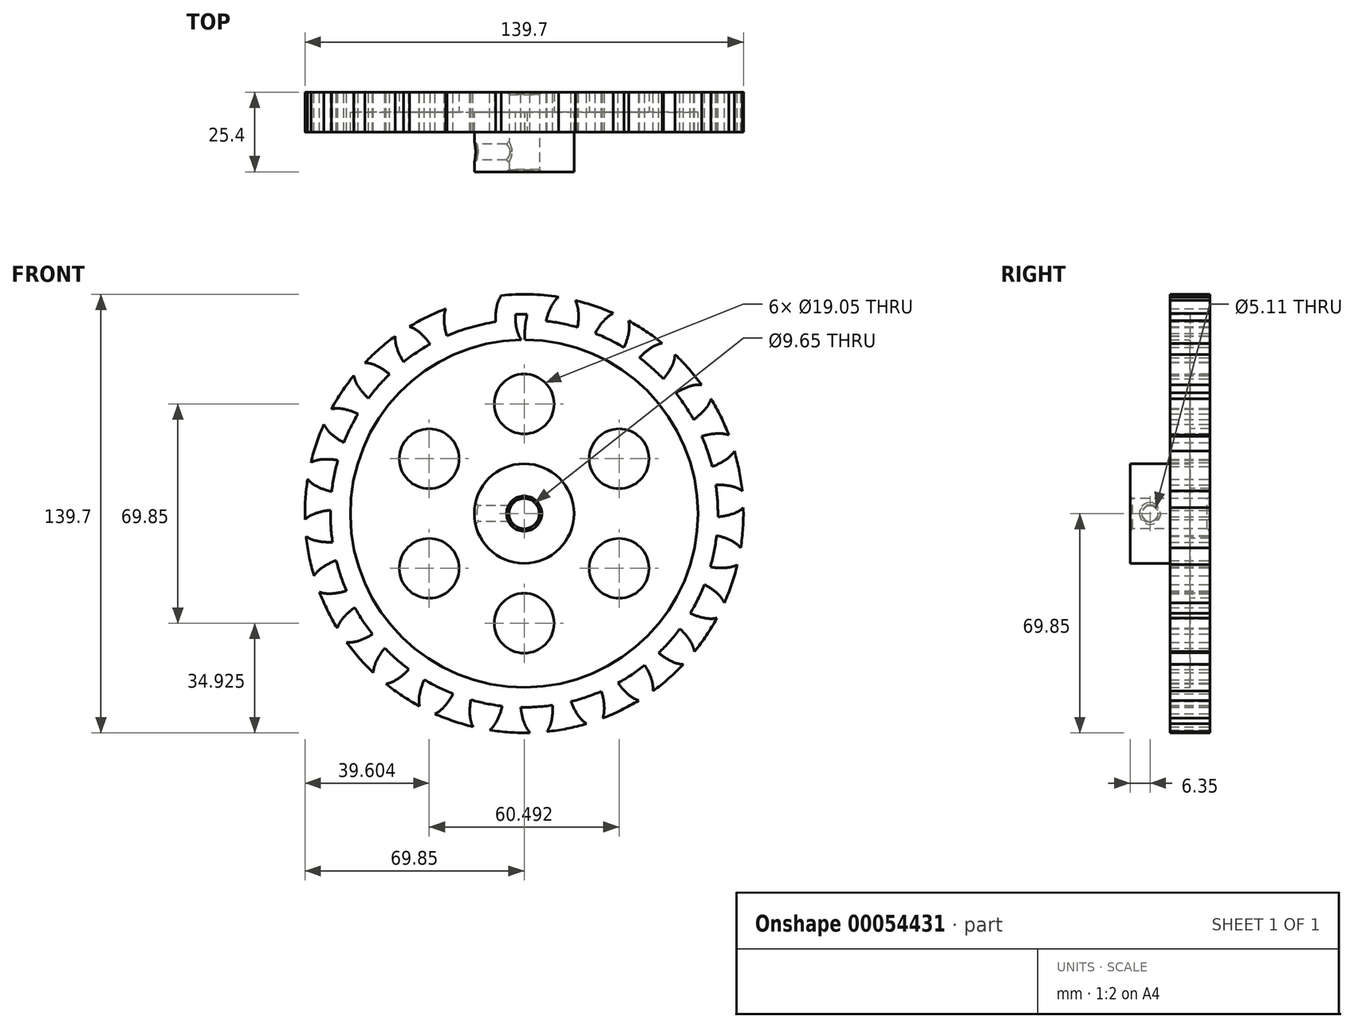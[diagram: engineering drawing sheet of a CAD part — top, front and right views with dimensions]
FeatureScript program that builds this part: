
annotation { "Feature Type Name" : "Feature", "Feature Type Description" : "" }
export const myFeature = defineFeature(function(context is Context, id is Id, definition is map)
    precondition{}
    {
        {
            var Q0;
            Q0=qCreatedBy(makeId("Front.planeOp"),FACE);
            var sketch = newSketch(context, id + "F0", { "sketchPlane" : qUnion([Q0])});
            skCircle(sketch, "E0", {"center": v(0, 0) * mm, "radius": 69.85 * mm});
            skCircle(sketch, "E1", {"center": v(0, 0) * mm, "radius": 66.68 * mm, "construction": true});
            skCircle(sketch, "E2", {"center": v(0, 0) * mm, "radius": 61.72 * mm});
            skLineSegment(sketch, "E3", {"start": v(0, 0) * mm, "end": v(0, 175.81) * mm, "construction": true});
            skLineSegment(sketch, "E4", {"start": v(0, 0) * mm, "end": v(-11.52, 175.81) * mm, "construction": true});
            skLineSegment(sketch, "E5", {"start": v(0, 66.68) * mm, "end": v(-79.4, 66.68) * mm, "construction": true});
            skLineSegment(sketch, "E6", {"start": v(0, 66.68) * mm, "end": v(-79.4, 37.77) * mm, "construction": true});
            skCircle(sketch, "E7", {"center": v(0, 0) * mm, "radius": 62.65 * mm, "construction": true});
            skCircle(sketch, "E8", {"center": v(0, 66.68) * mm, "radius": 13.65 * mm, "construction": true});
            skCircle(sketch, "E9", {"center": v(-12.58, 61.38) * mm, "radius": 13.65 * mm, "construction": true});
            skArc(sketch, "E10", {"start": v(0, 66.68) * mm, "mid": v(-0.78, 68.34) * mm, "end": v(-1.86, 69.83) * mm});
            skArc(sketch, "E11", {"start": v(1.07, 61.71) * mm, "mid": v(0.7, 64.23) * mm, "end": v(0, 66.68) * mm});
            skArc(sketch, "E12.MirrorCS", {"start": v(-8.7, 66.1) * mm, "mid": v(-8.15, 67.86) * mm, "end": v(-7.27, 69.47) * mm});
            skArc(sketch, "E13.MirrorCS", {"start": v(-9.11, 61.05) * mm, "mid": v(-9.07, 63.59) * mm, "end": v(-8.7, 66.1) * mm});
            skArc(sketch, "E14", {"start": v(-2.14, 70.13) * mm, "mid": v(-4.7, 69.8) * mm, "end": v(-7.27, 69.47) * mm});
            skArc(sketch, "E15.1.0", {"start": v(-25.52, 61.6) * mm, "mid": v(-25.43, 63.43) * mm, "end": v(-25, 65.22) * mm});
            skArc(sketch, "E15.1.1", {"start": v(-24.6, 56.6) * mm, "mid": v(-25.22, 59.07) * mm, "end": v(-25.52, 61.6) * mm});
            skArc(sketch, "E15.1.2", {"start": v(-20.22, 67.19) * mm, "mid": v(-22.61, 66.2) * mm, "end": v(-25, 65.22) * mm});
            skArc(sketch, "E15.1.3", {"start": v(-17.26, 64.4) * mm, "mid": v(-18.44, 65.8) * mm, "end": v(-19.87, 66.97) * mm});
            skArc(sketch, "E15.1.4", {"start": v(-14.94, 59.89) * mm, "mid": v(-15.95, 62.22) * mm, "end": v(-17.26, 64.4) * mm});
            skArc(sketch, "E15.2.0", {"start": v(-40.59, 52.9) * mm, "mid": v(-40.98, 54.7) * mm, "end": v(-41.03, 56.53) * mm});
            skArc(sketch, "E15.2.1", {"start": v(-38.41, 48.31) * mm, "mid": v(-39.65, 50.53) * mm, "end": v(-40.59, 52.9) * mm});
            skArc(sketch, "E15.2.2", {"start": v(-36.92, 59.66) * mm, "mid": v(-38.98, 58.1) * mm, "end": v(-41.03, 56.53) * mm});
            skArc(sketch, "E15.2.3", {"start": v(-33.34, 57.74) * mm, "mid": v(-34.84, 58.8) * mm, "end": v(-36.52, 59.54) * mm});
            skArc(sketch, "E15.2.4", {"start": v(-29.93, 53.98) * mm, "mid": v(-31.51, 55.97) * mm, "end": v(-33.34, 57.74) * mm});
            skArc(sketch, "E15.3.0", {"start": v(-52.9, 40.59) * mm, "mid": v(-53.74, 42.22) * mm, "end": v(-54.27, 43.98) * mm});
            skArc(sketch, "E15.3.1", {"start": v(-49.6, 36.72) * mm, "mid": v(-51.38, 38.55) * mm, "end": v(-52.9, 40.59) * mm});
            skArc(sketch, "E15.3.2", {"start": v(-51.1, 48.08) * mm, "mid": v(-52.69, 46.03) * mm, "end": v(-54.27, 43.98) * mm});
            skArc(sketch, "E15.3.3", {"start": v(-47.15, 47.15) * mm, "mid": v(-48.87, 47.77) * mm, "end": v(-50.69, 48.06) * mm});
            skArc(sketch, "E15.3.4", {"start": v(-42.88, 44.4) * mm, "mid": v(-44.93, 45.9) * mm, "end": v(-47.15, 47.15) * mm});
            skArc(sketch, "E15.4.0", {"start": v(-61.6, 25.52) * mm, "mid": v(-62.84, 26.87) * mm, "end": v(-63.8, 28.44) * mm});
            skArc(sketch, "E15.4.1", {"start": v(-57.42, 22.63) * mm, "mid": v(-59.6, 23.94) * mm, "end": v(-61.6, 25.52) * mm});
            skArc(sketch, "E15.4.2", {"start": v(-61.8, 33.21) * mm, "mid": v(-62.8, 30.83) * mm, "end": v(-63.8, 28.44) * mm});
            skArc(sketch, "E15.4.3", {"start": v(-57.74, 33.34) * mm, "mid": v(-59.57, 33.5) * mm, "end": v(-61.4, 33.3) * mm});
            skArc(sketch, "E15.4.4", {"start": v(-52.91, 31.78) * mm, "mid": v(-55.28, 32.72) * mm, "end": v(-57.74, 33.34) * mm});
            skArc(sketch, "E15.5.0", {"start": v(-66.1, 8.7) * mm, "mid": v(-67.65, 9.7) * mm, "end": v(-68.99, 10.96) * mm});
            skArc(sketch, "E15.5.1", {"start": v(-61.32, 7) * mm, "mid": v(-63.77, 7.7) * mm, "end": v(-66.1, 8.7) * mm});
            skArc(sketch, "E15.5.2", {"start": v(-68.3, 16.09) * mm, "mid": v(-68.65, 13.52) * mm, "end": v(-68.99, 10.96) * mm});
            skArc(sketch, "E15.5.3", {"start": v(-64.4, 17.26) * mm, "mid": v(-66.21, 16.94) * mm, "end": v(-67.93, 16.28) * mm});
            skArc(sketch, "E15.5.4", {"start": v(-59.33, 17) * mm, "mid": v(-61.86, 17.3) * mm, "end": v(-64.4, 17.26) * mm});
            skArc(sketch, "E15.6.0", {"start": v(-66.1, -8.7) * mm, "mid": v(-67.86, -8.15) * mm, "end": v(-69.47, -7.27) * mm});
            skArc(sketch, "E15.6.1", {"start": v(-61.05, -9.11) * mm, "mid": v(-63.59, -9.07) * mm, "end": v(-66.1, -8.7) * mm});
            skArc(sketch, "E15.6.2", {"start": v(-70.13, -2.14) * mm, "mid": v(-69.8, -4.7) * mm, "end": v(-69.47, -7.27) * mm});
            skArc(sketch, "E15.6.3", {"start": v(-66.68, 0) * mm, "mid": v(-68.34, -0.78) * mm, "end": v(-69.83, -1.86) * mm});
            skArc(sketch, "E15.6.4", {"start": v(-61.71, 1.07) * mm, "mid": v(-64.23, 0.7) * mm, "end": v(-66.68, 0) * mm});
            skArc(sketch, "E15.7.0", {"start": v(-61.6, -25.52) * mm, "mid": v(-63.43, -25.43) * mm, "end": v(-65.22, -25) * mm});
            skArc(sketch, "E15.7.1", {"start": v(-56.6, -24.6) * mm, "mid": v(-59.07, -25.22) * mm, "end": v(-61.6, -25.52) * mm});
            skArc(sketch, "E15.7.2", {"start": v(-67.19, -20.22) * mm, "mid": v(-66.2, -22.61) * mm, "end": v(-65.22, -25) * mm});
            skArc(sketch, "E15.7.3", {"start": v(-64.4, -17.26) * mm, "mid": v(-65.8, -18.44) * mm, "end": v(-66.97, -19.87) * mm});
            skArc(sketch, "E15.7.4", {"start": v(-59.89, -14.94) * mm, "mid": v(-62.22, -15.95) * mm, "end": v(-64.4, -17.26) * mm});
            skArc(sketch, "E15.8.0", {"start": v(-52.9, -40.59) * mm, "mid": v(-54.7, -40.98) * mm, "end": v(-56.53, -41.03) * mm});
            skArc(sketch, "E15.8.1", {"start": v(-48.31, -38.41) * mm, "mid": v(-50.53, -39.65) * mm, "end": v(-52.9, -40.59) * mm});
            skArc(sketch, "E15.8.2", {"start": v(-59.66, -36.92) * mm, "mid": v(-58.1, -38.98) * mm, "end": v(-56.53, -41.03) * mm});
            skArc(sketch, "E15.8.3", {"start": v(-57.74, -33.34) * mm, "mid": v(-58.8, -34.84) * mm, "end": v(-59.54, -36.52) * mm});
            skArc(sketch, "E15.8.4", {"start": v(-53.98, -29.93) * mm, "mid": v(-55.97, -31.51) * mm, "end": v(-57.74, -33.34) * mm});
            skArc(sketch, "E15.9.0", {"start": v(-40.59, -52.9) * mm, "mid": v(-42.22, -53.74) * mm, "end": v(-43.98, -54.27) * mm});
            skArc(sketch, "E15.9.1", {"start": v(-36.72, -49.6) * mm, "mid": v(-38.55, -51.38) * mm, "end": v(-40.59, -52.9) * mm});
            skArc(sketch, "E15.9.2", {"start": v(-48.08, -51.1) * mm, "mid": v(-46.03, -52.69) * mm, "end": v(-43.98, -54.27) * mm});
            skArc(sketch, "E15.9.3", {"start": v(-47.15, -47.15) * mm, "mid": v(-47.77, -48.87) * mm, "end": v(-48.06, -50.69) * mm});
            skArc(sketch, "E15.9.4", {"start": v(-44.4, -42.88) * mm, "mid": v(-45.9, -44.93) * mm, "end": v(-47.15, -47.15) * mm});
            skArc(sketch, "E15.10.0", {"start": v(-25.52, -61.6) * mm, "mid": v(-26.87, -62.84) * mm, "end": v(-28.44, -63.8) * mm});
            skArc(sketch, "E15.10.1", {"start": v(-22.63, -57.42) * mm, "mid": v(-23.94, -59.6) * mm, "end": v(-25.52, -61.6) * mm});
            skArc(sketch, "E15.10.2", {"start": v(-33.21, -61.8) * mm, "mid": v(-30.83, -62.8) * mm, "end": v(-28.44, -63.8) * mm});
            skArc(sketch, "E15.10.3", {"start": v(-33.34, -57.74) * mm, "mid": v(-33.5, -59.57) * mm, "end": v(-33.3, -61.4) * mm});
            skArc(sketch, "E15.10.4", {"start": v(-31.78, -52.91) * mm, "mid": v(-32.72, -55.28) * mm, "end": v(-33.34, -57.74) * mm});
            skArc(sketch, "E15.11.0", {"start": v(-8.7, -66.1) * mm, "mid": v(-9.7, -67.65) * mm, "end": v(-10.96, -68.99) * mm});
            skArc(sketch, "E15.11.1", {"start": v(-7, -61.32) * mm, "mid": v(-7.7, -63.77) * mm, "end": v(-8.7, -66.1) * mm});
            skArc(sketch, "E15.11.2", {"start": v(-16.09, -68.3) * mm, "mid": v(-13.52, -68.65) * mm, "end": v(-10.96, -68.99) * mm});
            skArc(sketch, "E15.11.3", {"start": v(-17.26, -64.4) * mm, "mid": v(-16.94, -66.21) * mm, "end": v(-16.28, -67.93) * mm});
            skArc(sketch, "E15.11.4", {"start": v(-17, -59.33) * mm, "mid": v(-17.3, -61.86) * mm, "end": v(-17.26, -64.4) * mm});
            skArc(sketch, "E15.12.0", {"start": v(8.7, -66.1) * mm, "mid": v(8.15, -67.86) * mm, "end": v(7.27, -69.47) * mm});
            skArc(sketch, "E15.12.1", {"start": v(9.11, -61.05) * mm, "mid": v(9.07, -63.59) * mm, "end": v(8.7, -66.1) * mm});
            skArc(sketch, "E15.12.2", {"start": v(2.14, -70.13) * mm, "mid": v(4.7, -69.8) * mm, "end": v(7.27, -69.47) * mm});
            skArc(sketch, "E15.12.3", {"start": v(0, -66.68) * mm, "mid": v(0.78, -68.34) * mm, "end": v(1.86, -69.83) * mm});
            skArc(sketch, "E15.12.4", {"start": v(-1.07, -61.71) * mm, "mid": v(-0.7, -64.23) * mm, "end": v(0, -66.68) * mm});
            skArc(sketch, "E15.13.0", {"start": v(25.52, -61.6) * mm, "mid": v(25.43, -63.43) * mm, "end": v(25, -65.22) * mm});
            skArc(sketch, "E15.13.1", {"start": v(24.6, -56.6) * mm, "mid": v(25.22, -59.07) * mm, "end": v(25.52, -61.6) * mm});
            skArc(sketch, "E15.13.2", {"start": v(20.22, -67.19) * mm, "mid": v(22.61, -66.2) * mm, "end": v(25, -65.22) * mm});
            skArc(sketch, "E15.13.3", {"start": v(17.26, -64.4) * mm, "mid": v(18.44, -65.8) * mm, "end": v(19.87, -66.97) * mm});
            skArc(sketch, "E15.13.4", {"start": v(14.94, -59.89) * mm, "mid": v(15.95, -62.22) * mm, "end": v(17.26, -64.4) * mm});
            skArc(sketch, "E15.14.0", {"start": v(40.59, -52.9) * mm, "mid": v(40.98, -54.7) * mm, "end": v(41.03, -56.53) * mm});
            skArc(sketch, "E15.14.1", {"start": v(38.41, -48.31) * mm, "mid": v(39.65, -50.53) * mm, "end": v(40.59, -52.9) * mm});
            skArc(sketch, "E15.14.2", {"start": v(36.92, -59.66) * mm, "mid": v(38.98, -58.1) * mm, "end": v(41.03, -56.53) * mm});
            skArc(sketch, "E15.14.3", {"start": v(33.34, -57.74) * mm, "mid": v(34.84, -58.8) * mm, "end": v(36.52, -59.54) * mm});
            skArc(sketch, "E15.14.4", {"start": v(29.93, -53.98) * mm, "mid": v(31.51, -55.97) * mm, "end": v(33.34, -57.74) * mm});
            skArc(sketch, "E15.15.0", {"start": v(52.9, -40.59) * mm, "mid": v(53.74, -42.22) * mm, "end": v(54.27, -43.98) * mm});
            skArc(sketch, "E15.15.1", {"start": v(49.6, -36.72) * mm, "mid": v(51.38, -38.55) * mm, "end": v(52.9, -40.59) * mm});
            skArc(sketch, "E15.15.2", {"start": v(51.1, -48.08) * mm, "mid": v(52.69, -46.03) * mm, "end": v(54.27, -43.98) * mm});
            skArc(sketch, "E15.15.3", {"start": v(47.15, -47.15) * mm, "mid": v(48.87, -47.77) * mm, "end": v(50.69, -48.06) * mm});
            skArc(sketch, "E15.15.4", {"start": v(42.88, -44.4) * mm, "mid": v(44.93, -45.9) * mm, "end": v(47.15, -47.15) * mm});
            skArc(sketch, "E15.16.0", {"start": v(61.6, -25.52) * mm, "mid": v(62.84, -26.87) * mm, "end": v(63.8, -28.44) * mm});
            skArc(sketch, "E15.16.1", {"start": v(57.42, -22.63) * mm, "mid": v(59.6, -23.94) * mm, "end": v(61.6, -25.52) * mm});
            skArc(sketch, "E15.16.2", {"start": v(61.8, -33.21) * mm, "mid": v(62.8, -30.83) * mm, "end": v(63.8, -28.44) * mm});
            skArc(sketch, "E15.16.3", {"start": v(57.74, -33.34) * mm, "mid": v(59.57, -33.5) * mm, "end": v(61.4, -33.3) * mm});
            skArc(sketch, "E15.16.4", {"start": v(52.91, -31.78) * mm, "mid": v(55.28, -32.72) * mm, "end": v(57.74, -33.34) * mm});
            skArc(sketch, "E15.17.0", {"start": v(66.1, -8.7) * mm, "mid": v(67.65, -9.7) * mm, "end": v(68.99, -10.96) * mm});
            skArc(sketch, "E15.17.1", {"start": v(61.32, -7) * mm, "mid": v(63.77, -7.7) * mm, "end": v(66.1, -8.7) * mm});
            skArc(sketch, "E15.17.2", {"start": v(68.3, -16.09) * mm, "mid": v(68.65, -13.52) * mm, "end": v(68.99, -10.96) * mm});
            skArc(sketch, "E15.17.3", {"start": v(64.4, -17.26) * mm, "mid": v(66.21, -16.94) * mm, "end": v(67.93, -16.28) * mm});
            skArc(sketch, "E15.17.4", {"start": v(59.33, -17) * mm, "mid": v(61.86, -17.3) * mm, "end": v(64.4, -17.26) * mm});
            skArc(sketch, "E15.18.0", {"start": v(66.1, 8.7) * mm, "mid": v(67.86, 8.15) * mm, "end": v(69.47, 7.27) * mm});
            skArc(sketch, "E15.18.1", {"start": v(61.05, 9.11) * mm, "mid": v(63.59, 9.07) * mm, "end": v(66.1, 8.7) * mm});
            skArc(sketch, "E15.18.2", {"start": v(70.13, 2.14) * mm, "mid": v(69.8, 4.7) * mm, "end": v(69.47, 7.27) * mm});
            skArc(sketch, "E15.18.3", {"start": v(66.68, 0) * mm, "mid": v(68.34, 0.78) * mm, "end": v(69.83, 1.86) * mm});
            skArc(sketch, "E15.18.4", {"start": v(61.71, -1.07) * mm, "mid": v(64.23, -0.7) * mm, "end": v(66.68, 0) * mm});
            skArc(sketch, "E15.19.0", {"start": v(61.6, 25.52) * mm, "mid": v(63.43, 25.43) * mm, "end": v(65.22, 25) * mm});
            skArc(sketch, "E15.19.1", {"start": v(56.6, 24.6) * mm, "mid": v(59.07, 25.22) * mm, "end": v(61.6, 25.52) * mm});
            skArc(sketch, "E15.19.2", {"start": v(67.19, 20.22) * mm, "mid": v(66.2, 22.61) * mm, "end": v(65.22, 25) * mm});
            skArc(sketch, "E15.19.3", {"start": v(64.4, 17.26) * mm, "mid": v(65.8, 18.44) * mm, "end": v(66.97, 19.87) * mm});
            skArc(sketch, "E15.19.4", {"start": v(59.89, 14.94) * mm, "mid": v(62.22, 15.95) * mm, "end": v(64.4, 17.26) * mm});
            skArc(sketch, "E15.20.0", {"start": v(52.9, 40.59) * mm, "mid": v(54.7, 40.98) * mm, "end": v(56.53, 41.03) * mm});
            skArc(sketch, "E15.20.1", {"start": v(48.31, 38.41) * mm, "mid": v(50.53, 39.65) * mm, "end": v(52.9, 40.59) * mm});
            skArc(sketch, "E15.20.2", {"start": v(59.66, 36.92) * mm, "mid": v(58.1, 38.98) * mm, "end": v(56.53, 41.03) * mm});
            skArc(sketch, "E15.20.3", {"start": v(57.74, 33.34) * mm, "mid": v(58.8, 34.84) * mm, "end": v(59.54, 36.52) * mm});
            skArc(sketch, "E15.20.4", {"start": v(53.98, 29.93) * mm, "mid": v(55.97, 31.51) * mm, "end": v(57.74, 33.34) * mm});
            skArc(sketch, "E15.21.0", {"start": v(40.59, 52.9) * mm, "mid": v(42.22, 53.74) * mm, "end": v(43.98, 54.27) * mm});
            skArc(sketch, "E15.21.1", {"start": v(36.72, 49.6) * mm, "mid": v(38.55, 51.38) * mm, "end": v(40.59, 52.9) * mm});
            skArc(sketch, "E15.21.2", {"start": v(48.08, 51.1) * mm, "mid": v(46.03, 52.69) * mm, "end": v(43.98, 54.27) * mm});
            skArc(sketch, "E15.21.3", {"start": v(47.15, 47.15) * mm, "mid": v(47.77, 48.87) * mm, "end": v(48.06, 50.69) * mm});
            skArc(sketch, "E15.21.4", {"start": v(44.4, 42.88) * mm, "mid": v(45.9, 44.93) * mm, "end": v(47.15, 47.15) * mm});
            skArc(sketch, "E15.22.0", {"start": v(25.52, 61.6) * mm, "mid": v(26.87, 62.84) * mm, "end": v(28.44, 63.8) * mm});
            skArc(sketch, "E15.22.1", {"start": v(22.63, 57.42) * mm, "mid": v(23.94, 59.6) * mm, "end": v(25.52, 61.6) * mm});
            skArc(sketch, "E15.22.2", {"start": v(33.21, 61.8) * mm, "mid": v(30.83, 62.8) * mm, "end": v(28.44, 63.8) * mm});
            skArc(sketch, "E15.22.3", {"start": v(33.34, 57.74) * mm, "mid": v(33.5, 59.57) * mm, "end": v(33.3, 61.4) * mm});
            skArc(sketch, "E15.22.4", {"start": v(31.78, 52.91) * mm, "mid": v(32.72, 55.28) * mm, "end": v(33.34, 57.74) * mm});
            skArc(sketch, "E15.23.0", {"start": v(8.7, 66.1) * mm, "mid": v(9.7, 67.65) * mm, "end": v(10.96, 68.99) * mm});
            skArc(sketch, "E15.23.1", {"start": v(7, 61.32) * mm, "mid": v(7.7, 63.77) * mm, "end": v(8.7, 66.1) * mm});
            skArc(sketch, "E15.23.2", {"start": v(16.09, 68.3) * mm, "mid": v(13.52, 68.65) * mm, "end": v(10.96, 68.99) * mm});
            skArc(sketch, "E15.23.3", {"start": v(17.26, 64.4) * mm, "mid": v(16.94, 66.21) * mm, "end": v(16.28, 67.93) * mm});
            skArc(sketch, "E15.23.4", {"start": v(17, 59.33) * mm, "mid": v(17.3, 61.86) * mm, "end": v(17.26, 64.4) * mm});
            skSolve(sketch);
        }
        {
            var Q0;
            {var subQ0=sQuery(id+"F0.wireOp",EDGE,"E2");var subQ1=makeQuery(id+"F0.imprint","INTERSECT",VERTEX,{"derivedFrom":[subQ0,sQuery(id+"F0.wireOp",EDGE,"E11")]});Q0=makeQuery(id+"F0.imprint","IMPRINT",FACE,{"disambiguationData":[TD([[makeQuery(id+"F0.imprint","IMPRINT",EDGE,{"disambiguationData":[TD([[subQ1,-1.0]])],"derivedFrom":subQ0}),1.0]])]});}
            var Q1;
            {var subQ0=sQuery(id+"F0.wireOp",EDGE,"E11");Q1=makeQuery(id+"F0.imprint","IMPRINT",FACE,{"disambiguationData":[TD([[makeQuery(id+"F0.imprint","IMPRINT",EDGE,{"derivedFrom":subQ0}),1.0]])]});}
            var Q2;
            Q2=makeQuery(id+"F0.imprint","IMPRINT",FACE,{"disambiguationData":[TD([[makeQuery(id+"F0.imprint","IMPRINT",EDGE,{"derivedFrom":sQuery(id+"F0.wireOp",EDGE,"E15.1.0")}),-1.0]])]});
            var Q3;
            Q3=makeQuery(id+"F0.imprint","IMPRINT",FACE,{"disambiguationData":[TD([[makeQuery(id+"F0.imprint","IMPRINT",EDGE,{"derivedFrom":sQuery(id+"F0.wireOp",EDGE,"E15.2.0")}),-1.0]])]});
            var Q4;
            Q4=makeQuery(id+"F0.imprint","IMPRINT",FACE,{"disambiguationData":[TD([[makeQuery(id+"F0.imprint","IMPRINT",EDGE,{"derivedFrom":sQuery(id+"F0.wireOp",EDGE,"E15.3.0")}),-1.0]])]});
            var Q5;
            Q5=makeQuery(id+"F0.imprint","IMPRINT",FACE,{"disambiguationData":[TD([[makeQuery(id+"F0.imprint","IMPRINT",EDGE,{"derivedFrom":sQuery(id+"F0.wireOp",EDGE,"E15.4.0")}),-1.0]])]});
            var Q6;
            Q6=makeQuery(id+"F0.imprint","IMPRINT",FACE,{"disambiguationData":[TD([[makeQuery(id+"F0.imprint","IMPRINT",EDGE,{"derivedFrom":sQuery(id+"F0.wireOp",EDGE,"E15.5.0")}),-1.0]])]});
            var Q7;
            Q7=makeQuery(id+"F0.imprint","IMPRINT",FACE,{"disambiguationData":[TD([[makeQuery(id+"F0.imprint","IMPRINT",EDGE,{"derivedFrom":sQuery(id+"F0.wireOp",EDGE,"E15.6.0")}),-1.0]])]});
            var Q8;
            Q8=makeQuery(id+"F0.imprint","IMPRINT",FACE,{"disambiguationData":[TD([[makeQuery(id+"F0.imprint","IMPRINT",EDGE,{"derivedFrom":sQuery(id+"F0.wireOp",EDGE,"E15.7.0")}),-1.0]])]});
            var Q9;
            Q9=makeQuery(id+"F0.imprint","IMPRINT",FACE,{"disambiguationData":[TD([[makeQuery(id+"F0.imprint","IMPRINT",EDGE,{"derivedFrom":sQuery(id+"F0.wireOp",EDGE,"E15.8.0")}),-1.0]])]});
            var Q10;
            Q10=makeQuery(id+"F0.imprint","IMPRINT",FACE,{"disambiguationData":[TD([[makeQuery(id+"F0.imprint","IMPRINT",EDGE,{"derivedFrom":sQuery(id+"F0.wireOp",EDGE,"E15.9.0")}),-1.0]])]});
            var Q11;
            Q11=makeQuery(id+"F0.imprint","IMPRINT",FACE,{"disambiguationData":[TD([[makeQuery(id+"F0.imprint","IMPRINT",EDGE,{"derivedFrom":sQuery(id+"F0.wireOp",EDGE,"E15.10.0")}),-1.0]])]});
            var Q12;
            Q12=makeQuery(id+"F0.imprint","IMPRINT",FACE,{"disambiguationData":[TD([[makeQuery(id+"F0.imprint","IMPRINT",EDGE,{"derivedFrom":sQuery(id+"F0.wireOp",EDGE,"E15.11.0")}),-1.0]])]});
            var Q13;
            Q13=makeQuery(id+"F0.imprint","IMPRINT",FACE,{"disambiguationData":[TD([[makeQuery(id+"F0.imprint","IMPRINT",EDGE,{"derivedFrom":sQuery(id+"F0.wireOp",EDGE,"E15.12.0")}),-1.0]])]});
            var Q14;
            Q14=makeQuery(id+"F0.imprint","IMPRINT",FACE,{"disambiguationData":[TD([[makeQuery(id+"F0.imprint","IMPRINT",EDGE,{"derivedFrom":sQuery(id+"F0.wireOp",EDGE,"E15.13.0")}),-1.0]])]});
            var Q15;
            Q15=makeQuery(id+"F0.imprint","IMPRINT",FACE,{"disambiguationData":[TD([[makeQuery(id+"F0.imprint","IMPRINT",EDGE,{"derivedFrom":sQuery(id+"F0.wireOp",EDGE,"E15.14.0")}),-1.0]])]});
            var Q16;
            Q16=makeQuery(id+"F0.imprint","IMPRINT",FACE,{"disambiguationData":[TD([[makeQuery(id+"F0.imprint","IMPRINT",EDGE,{"derivedFrom":sQuery(id+"F0.wireOp",EDGE,"E15.15.0")}),-1.0]])]});
            var Q17;
            Q17=makeQuery(id+"F0.imprint","IMPRINT",FACE,{"disambiguationData":[TD([[makeQuery(id+"F0.imprint","IMPRINT",EDGE,{"derivedFrom":sQuery(id+"F0.wireOp",EDGE,"E15.16.0")}),-1.0]])]});
            var Q18;
            Q18=makeQuery(id+"F0.imprint","IMPRINT",FACE,{"disambiguationData":[TD([[makeQuery(id+"F0.imprint","IMPRINT",EDGE,{"derivedFrom":sQuery(id+"F0.wireOp",EDGE,"E15.17.0")}),-1.0]])]});
            var Q19;
            Q19=makeQuery(id+"F0.imprint","IMPRINT",FACE,{"disambiguationData":[TD([[makeQuery(id+"F0.imprint","IMPRINT",EDGE,{"derivedFrom":sQuery(id+"F0.wireOp",EDGE,"E15.18.0")}),-1.0]])]});
            var Q20;
            Q20=makeQuery(id+"F0.imprint","IMPRINT",FACE,{"disambiguationData":[TD([[makeQuery(id+"F0.imprint","IMPRINT",EDGE,{"derivedFrom":sQuery(id+"F0.wireOp",EDGE,"E15.19.0")}),-1.0]])]});
            var Q21;
            Q21=makeQuery(id+"F0.imprint","IMPRINT",FACE,{"disambiguationData":[TD([[makeQuery(id+"F0.imprint","IMPRINT",EDGE,{"derivedFrom":sQuery(id+"F0.wireOp",EDGE,"E15.20.0")}),-1.0]])]});
            var Q22;
            Q22=makeQuery(id+"F0.imprint","IMPRINT",FACE,{"disambiguationData":[TD([[makeQuery(id+"F0.imprint","IMPRINT",EDGE,{"derivedFrom":sQuery(id+"F0.wireOp",EDGE,"E15.21.0")}),-1.0]])]});
            var Q23;
            Q23=makeQuery(id+"F0.imprint","IMPRINT",FACE,{"disambiguationData":[TD([[makeQuery(id+"F0.imprint","IMPRINT",EDGE,{"derivedFrom":sQuery(id+"F0.wireOp",EDGE,"E15.22.0")}),-1.0]])]});
            var Q24;
            Q24=makeQuery(id+"F0.imprint","IMPRINT",FACE,{"disambiguationData":[TD([[makeQuery(id+"F0.imprint","IMPRINT",EDGE,{"derivedFrom":sQuery(id+"F0.wireOp",EDGE,"E15.23.0")}),-1.0]])]});
            var Q25;
            {var subQ3=sQuery(id+"F0.wireOp",EDGE,"E14");Q25=makeQuery(id+"F0.imprint","IMPRINT",FACE,{"disambiguationData":[TD([[makeQuery(id+"F0.imprint","IMPRINT",EDGE,{"derivedFrom":subQ3}),-1.0]])]});}
            var Q26;
            {var subQ0=sQuery(id+"F0.wireOp",EDGE,"E15.1.2");Q26=makeQuery(id+"F0.imprint","IMPRINT",FACE,{"disambiguationData":[TD([[makeQuery(id+"F0.imprint","IMPRINT",EDGE,{"derivedFrom":subQ0}),-1.0]])]});}
            var Q27;
            {var subQ0=sQuery(id+"F0.wireOp",EDGE,"E15.2.2");Q27=makeQuery(id+"F0.imprint","IMPRINT",FACE,{"disambiguationData":[TD([[makeQuery(id+"F0.imprint","IMPRINT",EDGE,{"derivedFrom":subQ0}),-1.0]])]});}
            var Q28;
            {var subQ0=sQuery(id+"F0.wireOp",EDGE,"E15.3.2");Q28=makeQuery(id+"F0.imprint","IMPRINT",FACE,{"disambiguationData":[TD([[makeQuery(id+"F0.imprint","IMPRINT",EDGE,{"derivedFrom":subQ0}),-1.0]])]});}
            var Q29;
            {var subQ0=sQuery(id+"F0.wireOp",EDGE,"E15.4.2");Q29=makeQuery(id+"F0.imprint","IMPRINT",FACE,{"disambiguationData":[TD([[makeQuery(id+"F0.imprint","IMPRINT",EDGE,{"derivedFrom":subQ0}),-1.0]])]});}
            var Q30;
            {var subQ0=sQuery(id+"F0.wireOp",EDGE,"E15.5.2");Q30=makeQuery(id+"F0.imprint","IMPRINT",FACE,{"disambiguationData":[TD([[makeQuery(id+"F0.imprint","IMPRINT",EDGE,{"derivedFrom":subQ0}),-1.0]])]});}
            var Q31;
            {var subQ0=sQuery(id+"F0.wireOp",EDGE,"E15.6.2");Q31=makeQuery(id+"F0.imprint","IMPRINT",FACE,{"disambiguationData":[TD([[makeQuery(id+"F0.imprint","IMPRINT",EDGE,{"derivedFrom":subQ0}),-1.0]])]});}
            var Q32;
            {var subQ0=sQuery(id+"F0.wireOp",EDGE,"E15.7.2");Q32=makeQuery(id+"F0.imprint","IMPRINT",FACE,{"disambiguationData":[TD([[makeQuery(id+"F0.imprint","IMPRINT",EDGE,{"derivedFrom":subQ0}),-1.0]])]});}
            var Q33;
            {var subQ0=sQuery(id+"F0.wireOp",EDGE,"E15.8.2");Q33=makeQuery(id+"F0.imprint","IMPRINT",FACE,{"disambiguationData":[TD([[makeQuery(id+"F0.imprint","IMPRINT",EDGE,{"derivedFrom":subQ0}),-1.0]])]});}
            var Q34;
            {var subQ0=sQuery(id+"F0.wireOp",EDGE,"E15.9.2");Q34=makeQuery(id+"F0.imprint","IMPRINT",FACE,{"disambiguationData":[TD([[makeQuery(id+"F0.imprint","IMPRINT",EDGE,{"derivedFrom":subQ0}),-1.0]])]});}
            var Q35;
            {var subQ0=sQuery(id+"F0.wireOp",EDGE,"E15.10.2");Q35=makeQuery(id+"F0.imprint","IMPRINT",FACE,{"disambiguationData":[TD([[makeQuery(id+"F0.imprint","IMPRINT",EDGE,{"derivedFrom":subQ0}),-1.0]])]});}
            var Q36;
            {var subQ0=sQuery(id+"F0.wireOp",EDGE,"E15.11.2");Q36=makeQuery(id+"F0.imprint","IMPRINT",FACE,{"disambiguationData":[TD([[makeQuery(id+"F0.imprint","IMPRINT",EDGE,{"derivedFrom":subQ0}),-1.0]])]});}
            var Q37;
            {var subQ0=sQuery(id+"F0.wireOp",EDGE,"E15.12.2");Q37=makeQuery(id+"F0.imprint","IMPRINT",FACE,{"disambiguationData":[TD([[makeQuery(id+"F0.imprint","IMPRINT",EDGE,{"derivedFrom":subQ0}),-1.0]])]});}
            var Q38;
            {var subQ0=sQuery(id+"F0.wireOp",EDGE,"E15.13.2");Q38=makeQuery(id+"F0.imprint","IMPRINT",FACE,{"disambiguationData":[TD([[makeQuery(id+"F0.imprint","IMPRINT",EDGE,{"derivedFrom":subQ0}),-1.0]])]});}
            var Q39;
            {var subQ0=sQuery(id+"F0.wireOp",EDGE,"E15.14.2");Q39=makeQuery(id+"F0.imprint","IMPRINT",FACE,{"disambiguationData":[TD([[makeQuery(id+"F0.imprint","IMPRINT",EDGE,{"derivedFrom":subQ0}),-1.0]])]});}
            var Q40;
            {var subQ0=sQuery(id+"F0.wireOp",EDGE,"E15.15.2");Q40=makeQuery(id+"F0.imprint","IMPRINT",FACE,{"disambiguationData":[TD([[makeQuery(id+"F0.imprint","IMPRINT",EDGE,{"derivedFrom":subQ0}),-1.0]])]});}
            var Q41;
            {var subQ0=sQuery(id+"F0.wireOp",EDGE,"E15.16.2");Q41=makeQuery(id+"F0.imprint","IMPRINT",FACE,{"disambiguationData":[TD([[makeQuery(id+"F0.imprint","IMPRINT",EDGE,{"derivedFrom":subQ0}),-1.0]])]});}
            var Q42;
            {var subQ0=sQuery(id+"F0.wireOp",EDGE,"E15.17.2");Q42=makeQuery(id+"F0.imprint","IMPRINT",FACE,{"disambiguationData":[TD([[makeQuery(id+"F0.imprint","IMPRINT",EDGE,{"derivedFrom":subQ0}),-1.0]])]});}
            var Q43;
            {var subQ0=sQuery(id+"F0.wireOp",EDGE,"E15.18.2");Q43=makeQuery(id+"F0.imprint","IMPRINT",FACE,{"disambiguationData":[TD([[makeQuery(id+"F0.imprint","IMPRINT",EDGE,{"derivedFrom":subQ0}),-1.0]])]});}
            var Q44;
            {var subQ0=sQuery(id+"F0.wireOp",EDGE,"E15.19.2");Q44=makeQuery(id+"F0.imprint","IMPRINT",FACE,{"disambiguationData":[TD([[makeQuery(id+"F0.imprint","IMPRINT",EDGE,{"derivedFrom":subQ0}),-1.0]])]});}
            var Q45;
            {var subQ0=sQuery(id+"F0.wireOp",EDGE,"E15.20.2");Q45=makeQuery(id+"F0.imprint","IMPRINT",FACE,{"disambiguationData":[TD([[makeQuery(id+"F0.imprint","IMPRINT",EDGE,{"derivedFrom":subQ0}),-1.0]])]});}
            var Q46;
            {var subQ0=sQuery(id+"F0.wireOp",EDGE,"E15.21.2");Q46=makeQuery(id+"F0.imprint","IMPRINT",FACE,{"disambiguationData":[TD([[makeQuery(id+"F0.imprint","IMPRINT",EDGE,{"derivedFrom":subQ0}),-1.0]])]});}
            var Q47;
            {var subQ0=sQuery(id+"F0.wireOp",EDGE,"E15.22.2");Q47=makeQuery(id+"F0.imprint","IMPRINT",FACE,{"disambiguationData":[TD([[makeQuery(id+"F0.imprint","IMPRINT",EDGE,{"derivedFrom":subQ0}),-1.0]])]});}
            var Q48;
            {var subQ0=sQuery(id+"F0.wireOp",EDGE,"E15.23.2");Q48=makeQuery(id+"F0.imprint","IMPRINT",FACE,{"disambiguationData":[TD([[makeQuery(id+"F0.imprint","IMPRINT",EDGE,{"derivedFrom":subQ0}),-1.0]])]});}
            extrude(context, id + "F1", {"entities" : qUnion([Q0, Q1, Q2, Q3, Q4, Q5, Q6, Q7, Q8, Q9, Q10, Q11, Q12, Q13, Q14, Q15, Q16, Q17, Q18, Q19, Q20, Q21, Q22, Q23, Q24, Q25, Q26, Q27, Q28, Q29, Q30, Q31, Q32, Q33, Q34, Q35, Q36, Q37, Q38, Q39, Q40, Q41, Q42, Q43, Q44, Q45, Q46, Q47, Q48]), "depth" : 12.7 * mm});
        }
        {
            var Q0;
            Q0=makeQuery(id+"F1.opExtrude","CAP_FACE",FACE,{"disambiguationData":[OSD([sQuery(id+"F0.wireOp",EDGE,"E0"),sQuery(id+"F0.wireOp",EDGE,"E2"),sQuery(id+"F0.wireOp",EDGE,"E10"),sQuery(id+"F0.wireOp",EDGE,"E11"),sQuery(id+"F0.wireOp",EDGE,"E12.MirrorCS"),sQuery(id+"F0.wireOp",EDGE,"E13.MirrorCS"),sQuery(id+"F0.wireOp",EDGE,"E15.1.0"),sQuery(id+"F0.wireOp",EDGE,"E15.1.1"),sQuery(id+"F0.wireOp",EDGE,"E15.1.3"),sQuery(id+"F0.wireOp",EDGE,"E15.1.4"),sQuery(id+"F0.wireOp",EDGE,"E15.2.0"),sQuery(id+"F0.wireOp",EDGE,"E15.2.1"),sQuery(id+"F0.wireOp",EDGE,"E15.2.3"),sQuery(id+"F0.wireOp",EDGE,"E15.2.4"),sQuery(id+"F0.wireOp",EDGE,"E15.3.0"),sQuery(id+"F0.wireOp",EDGE,"E15.3.1"),sQuery(id+"F0.wireOp",EDGE,"E15.3.3"),sQuery(id+"F0.wireOp",EDGE,"E15.3.4"),sQuery(id+"F0.wireOp",EDGE,"E15.4.0"),sQuery(id+"F0.wireOp",EDGE,"E15.4.1"),sQuery(id+"F0.wireOp",EDGE,"E15.4.3"),sQuery(id+"F0.wireOp",EDGE,"E15.4.4"),sQuery(id+"F0.wireOp",EDGE,"E15.5.0"),sQuery(id+"F0.wireOp",EDGE,"E15.5.1"),sQuery(id+"F0.wireOp",EDGE,"E15.5.3"),sQuery(id+"F0.wireOp",EDGE,"E15.5.4"),sQuery(id+"F0.wireOp",EDGE,"E15.6.0"),sQuery(id+"F0.wireOp",EDGE,"E15.6.1"),sQuery(id+"F0.wireOp",EDGE,"E15.6.3"),sQuery(id+"F0.wireOp",EDGE,"E15.6.4"),sQuery(id+"F0.wireOp",EDGE,"E15.7.0"),sQuery(id+"F0.wireOp",EDGE,"E15.7.1"),sQuery(id+"F0.wireOp",EDGE,"E15.7.3"),sQuery(id+"F0.wireOp",EDGE,"E15.7.4"),sQuery(id+"F0.wireOp",EDGE,"E15.8.0"),sQuery(id+"F0.wireOp",EDGE,"E15.8.1"),sQuery(id+"F0.wireOp",EDGE,"E15.8.3"),sQuery(id+"F0.wireOp",EDGE,"E15.8.4"),sQuery(id+"F0.wireOp",EDGE,"E15.9.0"),sQuery(id+"F0.wireOp",EDGE,"E15.9.1"),sQuery(id+"F0.wireOp",EDGE,"E15.9.3"),sQuery(id+"F0.wireOp",EDGE,"E15.9.4"),sQuery(id+"F0.wireOp",EDGE,"E15.10.0"),sQuery(id+"F0.wireOp",EDGE,"E15.10.1"),sQuery(id+"F0.wireOp",EDGE,"E15.10.3"),sQuery(id+"F0.wireOp",EDGE,"E15.10.4"),sQuery(id+"F0.wireOp",EDGE,"E15.11.0"),sQuery(id+"F0.wireOp",EDGE,"E15.11.1"),sQuery(id+"F0.wireOp",EDGE,"E15.11.3"),sQuery(id+"F0.wireOp",EDGE,"E15.11.4"),sQuery(id+"F0.wireOp",EDGE,"E15.12.0"),sQuery(id+"F0.wireOp",EDGE,"E15.12.1"),sQuery(id+"F0.wireOp",EDGE,"E15.12.3"),sQuery(id+"F0.wireOp",EDGE,"E15.12.4"),sQuery(id+"F0.wireOp",EDGE,"E15.13.0"),sQuery(id+"F0.wireOp",EDGE,"E15.13.1"),sQuery(id+"F0.wireOp",EDGE,"E15.13.3"),sQuery(id+"F0.wireOp",EDGE,"E15.13.4"),sQuery(id+"F0.wireOp",EDGE,"E15.14.0"),sQuery(id+"F0.wireOp",EDGE,"E15.14.1"),sQuery(id+"F0.wireOp",EDGE,"E15.14.3"),sQuery(id+"F0.wireOp",EDGE,"E15.14.4"),sQuery(id+"F0.wireOp",EDGE,"E15.15.0"),sQuery(id+"F0.wireOp",EDGE,"E15.15.1"),sQuery(id+"F0.wireOp",EDGE,"E15.15.3"),sQuery(id+"F0.wireOp",EDGE,"E15.15.4"),sQuery(id+"F0.wireOp",EDGE,"E15.16.0"),sQuery(id+"F0.wireOp",EDGE,"E15.16.1"),sQuery(id+"F0.wireOp",EDGE,"E15.16.3"),sQuery(id+"F0.wireOp",EDGE,"E15.16.4"),sQuery(id+"F0.wireOp",EDGE,"E15.17.0"),sQuery(id+"F0.wireOp",EDGE,"E15.17.1"),sQuery(id+"F0.wireOp",EDGE,"E15.17.3"),sQuery(id+"F0.wireOp",EDGE,"E15.17.4"),sQuery(id+"F0.wireOp",EDGE,"E15.18.0"),sQuery(id+"F0.wireOp",EDGE,"E15.18.1"),sQuery(id+"F0.wireOp",EDGE,"E15.18.3"),sQuery(id+"F0.wireOp",EDGE,"E15.18.4"),sQuery(id+"F0.wireOp",EDGE,"E15.19.0"),sQuery(id+"F0.wireOp",EDGE,"E15.19.1"),sQuery(id+"F0.wireOp",EDGE,"E15.19.3"),sQuery(id+"F0.wireOp",EDGE,"E15.19.4"),sQuery(id+"F0.wireOp",EDGE,"E15.20.0"),sQuery(id+"F0.wireOp",EDGE,"E15.20.1"),sQuery(id+"F0.wireOp",EDGE,"E15.20.3"),sQuery(id+"F0.wireOp",EDGE,"E15.20.4"),sQuery(id+"F0.wireOp",EDGE,"E15.21.0"),sQuery(id+"F0.wireOp",EDGE,"E15.21.1"),sQuery(id+"F0.wireOp",EDGE,"E15.21.3"),sQuery(id+"F0.wireOp",EDGE,"E15.21.4"),sQuery(id+"F0.wireOp",EDGE,"E15.22.0"),sQuery(id+"F0.wireOp",EDGE,"E15.22.1"),sQuery(id+"F0.wireOp",EDGE,"E15.22.3"),sQuery(id+"F0.wireOp",EDGE,"E15.22.4"),sQuery(id+"F0.wireOp",EDGE,"E15.23.0"),sQuery(id+"F0.wireOp",EDGE,"E15.23.1"),sQuery(id+"F0.wireOp",EDGE,"E15.23.3"),sQuery(id+"F0.wireOp",EDGE,"E15.23.4")])],"isStart":false});
            shell(context, id + "F2", {"entities" : qUnion([Q0]), "thickness" : 6.35 * mm});
        }
        {
            var Q0;
            Q0=makeQuery(id+"F2.opShell","OFFSET_FACE",FACE,{"disambiguationData":[OSD([sQuery(id+"F0.wireOp",EDGE,"E0"),sQuery(id+"F0.wireOp",EDGE,"E2"),sQuery(id+"F0.wireOp",EDGE,"E10"),sQuery(id+"F0.wireOp",EDGE,"E11"),sQuery(id+"F0.wireOp",EDGE,"E12.MirrorCS"),sQuery(id+"F0.wireOp",EDGE,"E13.MirrorCS"),sQuery(id+"F0.wireOp",EDGE,"E15.1.0"),sQuery(id+"F0.wireOp",EDGE,"E15.1.1"),sQuery(id+"F0.wireOp",EDGE,"E15.1.3"),sQuery(id+"F0.wireOp",EDGE,"E15.1.4"),sQuery(id+"F0.wireOp",EDGE,"E15.2.0"),sQuery(id+"F0.wireOp",EDGE,"E15.2.1"),sQuery(id+"F0.wireOp",EDGE,"E15.2.3"),sQuery(id+"F0.wireOp",EDGE,"E15.2.4"),sQuery(id+"F0.wireOp",EDGE,"E15.3.0"),sQuery(id+"F0.wireOp",EDGE,"E15.3.1"),sQuery(id+"F0.wireOp",EDGE,"E15.3.3"),sQuery(id+"F0.wireOp",EDGE,"E15.3.4"),sQuery(id+"F0.wireOp",EDGE,"E15.4.0"),sQuery(id+"F0.wireOp",EDGE,"E15.4.1"),sQuery(id+"F0.wireOp",EDGE,"E15.4.3"),sQuery(id+"F0.wireOp",EDGE,"E15.4.4"),sQuery(id+"F0.wireOp",EDGE,"E15.5.0"),sQuery(id+"F0.wireOp",EDGE,"E15.5.1"),sQuery(id+"F0.wireOp",EDGE,"E15.5.3"),sQuery(id+"F0.wireOp",EDGE,"E15.5.4"),sQuery(id+"F0.wireOp",EDGE,"E15.6.0"),sQuery(id+"F0.wireOp",EDGE,"E15.6.1"),sQuery(id+"F0.wireOp",EDGE,"E15.6.3"),sQuery(id+"F0.wireOp",EDGE,"E15.6.4"),sQuery(id+"F0.wireOp",EDGE,"E15.7.0"),sQuery(id+"F0.wireOp",EDGE,"E15.7.1"),sQuery(id+"F0.wireOp",EDGE,"E15.7.3"),sQuery(id+"F0.wireOp",EDGE,"E15.7.4"),sQuery(id+"F0.wireOp",EDGE,"E15.8.0"),sQuery(id+"F0.wireOp",EDGE,"E15.8.1"),sQuery(id+"F0.wireOp",EDGE,"E15.8.3"),sQuery(id+"F0.wireOp",EDGE,"E15.8.4"),sQuery(id+"F0.wireOp",EDGE,"E15.9.0"),sQuery(id+"F0.wireOp",EDGE,"E15.9.1"),sQuery(id+"F0.wireOp",EDGE,"E15.9.3"),sQuery(id+"F0.wireOp",EDGE,"E15.9.4"),sQuery(id+"F0.wireOp",EDGE,"E15.10.0"),sQuery(id+"F0.wireOp",EDGE,"E15.10.1"),sQuery(id+"F0.wireOp",EDGE,"E15.10.3"),sQuery(id+"F0.wireOp",EDGE,"E15.10.4"),sQuery(id+"F0.wireOp",EDGE,"E15.11.0"),sQuery(id+"F0.wireOp",EDGE,"E15.11.1"),sQuery(id+"F0.wireOp",EDGE,"E15.11.3"),sQuery(id+"F0.wireOp",EDGE,"E15.11.4"),sQuery(id+"F0.wireOp",EDGE,"E15.12.0"),sQuery(id+"F0.wireOp",EDGE,"E15.12.1"),sQuery(id+"F0.wireOp",EDGE,"E15.12.3"),sQuery(id+"F0.wireOp",EDGE,"E15.12.4"),sQuery(id+"F0.wireOp",EDGE,"E15.13.0"),sQuery(id+"F0.wireOp",EDGE,"E15.13.1"),sQuery(id+"F0.wireOp",EDGE,"E15.13.3"),sQuery(id+"F0.wireOp",EDGE,"E15.13.4"),sQuery(id+"F0.wireOp",EDGE,"E15.14.0"),sQuery(id+"F0.wireOp",EDGE,"E15.14.1"),sQuery(id+"F0.wireOp",EDGE,"E15.14.3"),sQuery(id+"F0.wireOp",EDGE,"E15.14.4"),sQuery(id+"F0.wireOp",EDGE,"E15.15.0"),sQuery(id+"F0.wireOp",EDGE,"E15.15.1"),sQuery(id+"F0.wireOp",EDGE,"E15.15.3"),sQuery(id+"F0.wireOp",EDGE,"E15.15.4"),sQuery(id+"F0.wireOp",EDGE,"E15.16.0"),sQuery(id+"F0.wireOp",EDGE,"E15.16.1"),sQuery(id+"F0.wireOp",EDGE,"E15.16.3"),sQuery(id+"F0.wireOp",EDGE,"E15.16.4"),sQuery(id+"F0.wireOp",EDGE,"E15.17.0"),sQuery(id+"F0.wireOp",EDGE,"E15.17.1"),sQuery(id+"F0.wireOp",EDGE,"E15.17.3"),sQuery(id+"F0.wireOp",EDGE,"E15.17.4"),sQuery(id+"F0.wireOp",EDGE,"E15.18.0"),sQuery(id+"F0.wireOp",EDGE,"E15.18.1"),sQuery(id+"F0.wireOp",EDGE,"E15.18.3"),sQuery(id+"F0.wireOp",EDGE,"E15.18.4"),sQuery(id+"F0.wireOp",EDGE,"E15.19.0"),sQuery(id+"F0.wireOp",EDGE,"E15.19.1"),sQuery(id+"F0.wireOp",EDGE,"E15.19.3"),sQuery(id+"F0.wireOp",EDGE,"E15.19.4"),sQuery(id+"F0.wireOp",EDGE,"E15.20.0"),sQuery(id+"F0.wireOp",EDGE,"E15.20.1"),sQuery(id+"F0.wireOp",EDGE,"E15.20.3"),sQuery(id+"F0.wireOp",EDGE,"E15.20.4"),sQuery(id+"F0.wireOp",EDGE,"E15.21.0"),sQuery(id+"F0.wireOp",EDGE,"E15.21.1"),sQuery(id+"F0.wireOp",EDGE,"E15.21.3"),sQuery(id+"F0.wireOp",EDGE,"E15.21.4"),sQuery(id+"F0.wireOp",EDGE,"E15.22.0"),sQuery(id+"F0.wireOp",EDGE,"E15.22.1"),sQuery(id+"F0.wireOp",EDGE,"E15.22.3"),sQuery(id+"F0.wireOp",EDGE,"E15.22.4"),sQuery(id+"F0.wireOp",EDGE,"E15.23.0"),sQuery(id+"F0.wireOp",EDGE,"E15.23.1"),sQuery(id+"F0.wireOp",EDGE,"E15.23.3"),sQuery(id+"F0.wireOp",EDGE,"E15.23.4")])]});
            var sketch = newSketch(context, id + "F3", { "sketchPlane" : qUnion([Q0])});
            skCircle(sketch, "E16", {"center": v(0, 0) * mm, "radius": 15.88 * mm});
            skSolve(sketch);
        }
        {
            var Q0;
            Q0=makeQuery(id+"F3.imprint","IMPRINT",FACE,{"disambiguationData":[TD([[makeQuery(id+"F3.imprint","IMPRINT",EDGE,{"derivedFrom":sQuery(id+"F3.wireOp",EDGE,"E16")}),1.0]])]});
            extrude(context, id + "F4", {"entities" : qUnion([Q0]), "operationType" : NewBodyOperationType.ADD, "depth" : 19.05 * mm});
        }
        {
            var Q0;
            Q0=makeQuery(id+"F4.opExtrude","CAP_FACE",FACE,{"disambiguationData":[OSD([sQuery(id+"F3.wireOp",EDGE,"E16")])],"isStart":false});
            var sketch = newSketch(context, id + "F5", { "sketchPlane" : qUnion([Q0])});
            skCircle(sketch, "E17", {"center": v(0, 0) * mm, "radius": 4.83 * mm});
            skCircle(sketch, "E18", {"center": v(0, 0) * mm, "radius": 34.93 * mm, "construction": true});
            skLineSegment(sketch, "E19", {"start": v(0, 56.07) * mm, "end": v(0, -55.35) * mm, "construction": true});
            skCircle(sketch, "E20", {"center": v(0, 34.93) * mm, "radius": 9.53 * mm});
            skCircle(sketch, "E21.1.0", {"center": v(-30.25, 17.46) * mm, "radius": 9.53 * mm});
            skCircle(sketch, "E21.2.0", {"center": v(-30.25, -17.46) * mm, "radius": 9.53 * mm});
            skCircle(sketch, "E21.3.0", {"center": v(0, -34.93) * mm, "radius": 9.53 * mm});
            skCircle(sketch, "E21.4.0", {"center": v(30.25, -17.46) * mm, "radius": 9.53 * mm});
            skCircle(sketch, "E21.5.0", {"center": v(30.25, 17.46) * mm, "radius": 9.53 * mm});
            skSolve(sketch);
        }
        {
            var Q0;
            Q0=makeQuery(id+"F5.imprint","IMPRINT",FACE,{"disambiguationData":[TD([[makeQuery(id+"F5.imprint","IMPRINT",EDGE,{"derivedFrom":sQuery(id+"F5.wireOp",EDGE,"E17")}),1.0]])]});
            extrude(context, id + "F6", {"entities" : qUnion([Q0]), "operationType" : NewBodyOperationType.REMOVE, "endBound" : BoundingType.THROUGH_ALL, "oppositeDirection" : true, "depth" : 25.4 * mm});
        }
        {
            var Q0;
            Q0=makeQuery(id+"F5.imprint","IMPRINT",FACE,{"disambiguationData":[TD([[makeQuery(id+"F5.imprint","IMPRINT",EDGE,{"derivedFrom":sQuery(id+"F5.wireOp",EDGE,"E20")}),1.0]])]});
            var Q1;
            Q1=makeQuery(id+"F5.imprint","IMPRINT",FACE,{"disambiguationData":[TD([[makeQuery(id+"F5.imprint","IMPRINT",EDGE,{"derivedFrom":sQuery(id+"F5.wireOp",EDGE,"E21.1.0")}),1.0]])]});
            var Q2;
            Q2=makeQuery(id+"F5.imprint","IMPRINT",FACE,{"disambiguationData":[TD([[makeQuery(id+"F5.imprint","IMPRINT",EDGE,{"derivedFrom":sQuery(id+"F5.wireOp",EDGE,"E21.2.0")}),1.0]])]});
            var Q3;
            Q3=makeQuery(id+"F5.imprint","IMPRINT",FACE,{"disambiguationData":[TD([[makeQuery(id+"F5.imprint","IMPRINT",EDGE,{"derivedFrom":sQuery(id+"F5.wireOp",EDGE,"E21.5.0")}),1.0]])]});
            var Q4;
            Q4=makeQuery(id+"F5.imprint","IMPRINT",FACE,{"disambiguationData":[TD([[makeQuery(id+"F5.imprint","IMPRINT",EDGE,{"derivedFrom":sQuery(id+"F5.wireOp",EDGE,"E21.4.0")}),1.0]])]});
            var Q5;
            Q5=makeQuery(id+"F5.imprint","IMPRINT",FACE,{"disambiguationData":[TD([[makeQuery(id+"F5.imprint","IMPRINT",EDGE,{"derivedFrom":sQuery(id+"F5.wireOp",EDGE,"E21.3.0")}),1.0]])]});
            extrude(context, id + "F7", {"entities" : qUnion([Q0, Q1, Q2, Q3, Q4, Q5]), "operationType" : NewBodyOperationType.REMOVE, "endBound" : BoundingType.THROUGH_ALL, "oppositeDirection" : true, "depth" : 25.4 * mm});
        }
        {
            var Q0;
            Q0=qCreatedBy(makeId("Right.planeOp"),FACE);
            cPlane(context, id + "F8", {"entities" : qUnion([Q0]), "cplaneType" : CPlaneType.OFFSET, "offset" : 15.88 * mm, "oppositeDirection" : true, "width" : 152.4 * mm, "height" : 152.4 * mm});
        }
        {
            var Q0;
            Q0=qCreatedBy(id+"F8.planeOp",FACE);
            var sketch = newSketch(context, id + "F9", { "sketchPlane" : qUnion([Q0])});
            skCircle(sketch, "E22", {"center": v(-19.05, 0) * mm, "radius": 2.55 * mm});
            skSolve(sketch);
        }
        {
            var Q0;
            Q0=makeQuery(id+"F9.imprint","IMPRINT",FACE,{"disambiguationData":[TD([[makeQuery(id+"F9.imprint","IMPRINT",EDGE,{"derivedFrom":sQuery(id+"F9.wireOp",EDGE,"E22")}),1.0]])]});
            extrude(context, id + "F10", {"entities" : qUnion([Q0]), "operationType" : NewBodyOperationType.REMOVE, "endBound" : BoundingType.UP_TO_NEXT, "depth" : 25.4 * mm});
        }
        {
            var Q0;
            Q0=makeQuery(id+"F10.boolean.opBoolean","COPY",FACE,{"derivedFrom":makeQuery(id+"F10.opExtrude","SWEPT_FACE",FACE,{"disambiguationData":[OSD([sQuery(id+"F9.wireOp",EDGE,"E22")])]})});
            var Q1;
            Q1=makeQuery(id+"F6.boolean.opBoolean","COPY",FACE,{"derivedFrom":makeQuery(id+"F6.opExtrude","SWEPT_FACE",FACE,{"disambiguationData":[OSD([sQuery(id+"F5.wireOp",EDGE,"E17")])]})});
            chamfer(context, id + "F11", {"entities" : qUnion([Q0, Q1]), "width" : 0.8 * mm, "tangentPropagation" : true});
        }
    });
